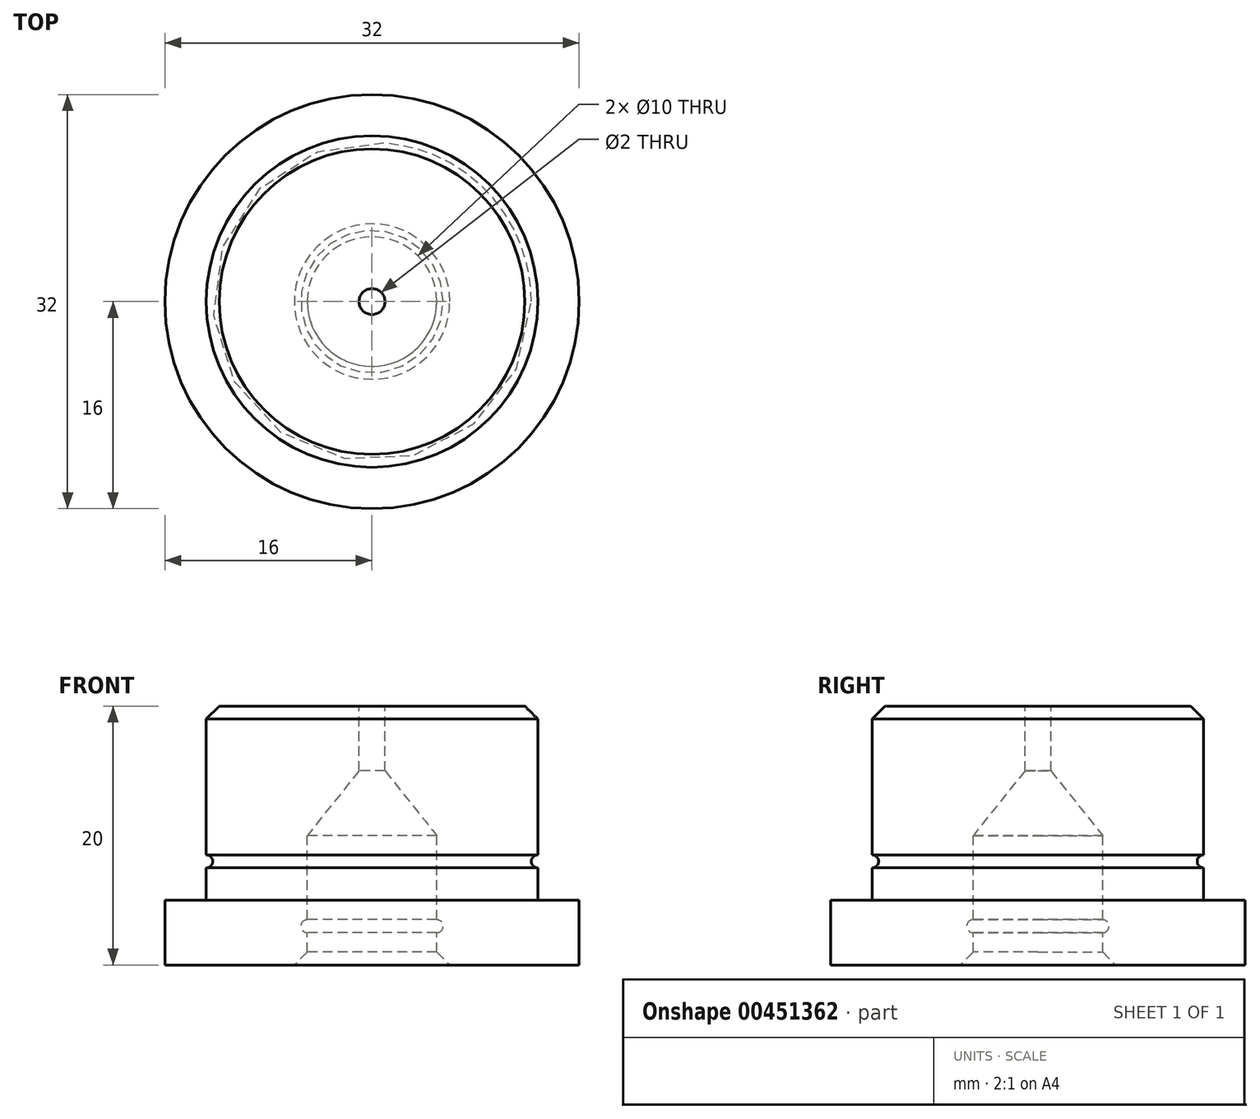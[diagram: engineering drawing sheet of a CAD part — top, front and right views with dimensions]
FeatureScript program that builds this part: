
annotation { "Feature Type Name" : "Feature", "Feature Type Description" : "" }
export const myFeature = defineFeature(function(context is Context, id is Id, definition is map)
    precondition{}
    {
        {
            var Q0;
            Q0=qCreatedBy(makeId("Front.planeOp"),FACE);
            var sketch = newSketch(context, id + "F0", { "sketchPlane" : qUnion([Q0])});
            skLineSegment(sketch, "E0", {"start": v(0, 0) * mm, "end": v(12.8, 0) * mm});
            skLineSegment(sketch, "E1", {"start": v(12.8, 0) * mm, "end": v(12.8, -15) * mm});
            skLineSegment(sketch, "E2", {"start": v(12.8, -15) * mm, "end": v(16, -15) * mm});
            skLineSegment(sketch, "E3", {"start": v(16, -15) * mm, "end": v(16, -20) * mm});
            skLineSegment(sketch, "E4", {"start": v(16, -20) * mm, "end": v(5, -20) * mm});
            skLineSegment(sketch, "E5", {"start": v(5, -20) * mm, "end": v(5, -10) * mm});
            skLineSegment(sketch, "E6", {"start": v(5, -10) * mm, "end": v(1, -5) * mm});
            skLineSegment(sketch, "E7", {"start": v(1, -5) * mm, "end": v(1, 0) * mm});
            skLineSegment(sketch, "E8", {"start": v(0, 0) * mm, "end": v(0, -32.89) * mm, "construction": true});
            skArc(sketch, "E9", {"start": v(5, -16.5) * mm, "mid": v(5.5, -17) * mm, "end": v(5, -17.5) * mm});
            skArc(sketch, "E10", {"start": v(12.8, -12.5) * mm, "mid": v(12.3, -12) * mm, "end": v(12.8, -11.5) * mm});
            skSolve(sketch);
        }
        {
            var Q0;
            {var subQ9=sQuery(id+"F0.wireOp",EDGE,"E2");Q0=makeQuery(id+"F0.imprint","IMPRINT",FACE,{"disambiguationData":[TD([[makeQuery(id+"F0.imprint","IMPRINT",EDGE,{"derivedFrom":subQ9}),-1.0]])]});}
            var Q1;
            Q1=sQuery(id+"F0.wireOp",EDGE,"E8");
            revolve(context, id + "F1", {"entities" : qUnion([Q0]), "axis" : qUnion([Q1]), "revolveType" : RevolveType.FULL});
        }
        {
            var Q0;
            Q0=makeQuery(id+"F1.opRevolve","SWEPT_EDGE",EDGE,{"disambiguationData":[OSD([sQuery(id+"F0.wireOp",EDGE,"E0"),sQuery(id+"F0.wireOp",EDGE,"E1")])]});
            chamfer(context, id + "F2", {"entities" : qUnion([Q0]), "width" : 1 * mm, "tangentPropagation" : true});
        }
        {
            var Q0;
            Q0=makeQuery(id+"F1.opRevolve","SWEPT_EDGE",EDGE,{"disambiguationData":[OSD([sQuery(id+"F0.wireOp",EDGE,"E4"),sQuery(id+"F0.wireOp",EDGE,"E5")])]});
            chamfer(context, id + "F3", {"entities" : qUnion([Q0]), "width" : 1 * mm, "tangentPropagation" : true});
        }
    });
